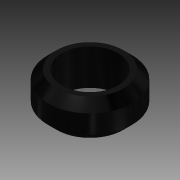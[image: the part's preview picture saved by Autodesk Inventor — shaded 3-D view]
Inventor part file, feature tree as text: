
AUTODESK INVENTOR PART (.ipt)
format: ipt  version: 2014 SP1 (Build 180222100, 222)  size: 92,160 bytes
history: native  units: in
note: dims shown in document units (in); Inventor stores cm internally (conversion verified against a paired STEP export)
features: revolve x1, sketch x1
ambient origin geometry x8: Origin, YZ Plane, XZ Plane, XY Plane, X Axis, Y Axis, Z Axis, Center Point
bodies: Solid1 (feature_tree)
feature tree (2):
  revolve  "Revolution1"  [1 undecoded]
  sketch  "Sketch1"  dims[d0=0.4028in d1=0.6289in d2=90.0deg d5=0.9409in d6=90.0deg d7=0.0591in]
note: 1 required parameter value undecoded (feature->parameter linkage not recoverable at this tier; creation-order binding heuristic only, values carry confidence <= 0.55)
